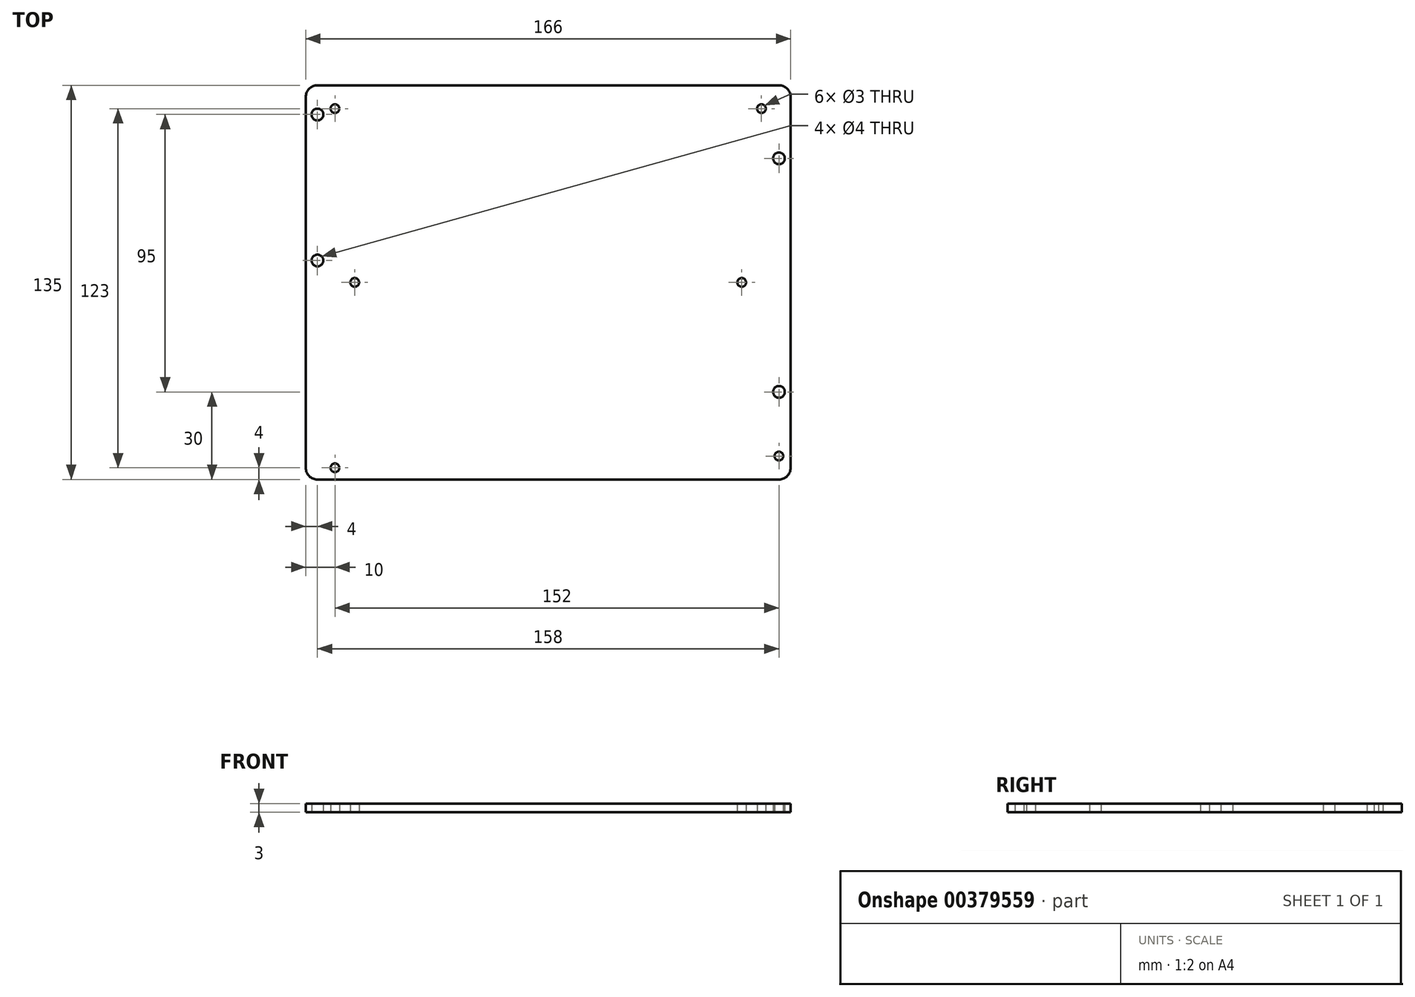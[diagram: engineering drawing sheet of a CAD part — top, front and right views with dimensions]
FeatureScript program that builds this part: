
annotation { "Feature Type Name" : "Feature", "Feature Type Description" : "" }
export const myFeature = defineFeature(function(context is Context, id is Id, definition is map)
    precondition{}
    {
        {
            var Q0;
            Q0=qCreatedBy(makeId("Top.planeOp"),FACE);
            var sketch = newSketch(context, id + "F0", { "sketchPlane" : qUnion([Q0])});
            skLineSegment(sketch, "E0.bottom", {"start": v(79, 67.5) * mm, "end": v(-79, 67.5) * mm});
            skLineSegment(sketch, "E0.top", {"start": v(79, -67.5) * mm, "end": v(-79, -67.5) * mm});
            skLineSegment(sketch, "E0.left", {"start": v(83, 63.5) * mm, "end": v(83, -63.5) * mm});
            skLineSegment(sketch, "E0.right", {"start": v(-83, 63.5) * mm, "end": v(-83, -63.5) * mm});
            skPoint(sketch, "E0.middle", {"position": v(0, 0) * mm});
            skLineSegment(sketch, "E1", {"start": v(0, 86.64) * mm, "end": v(0, -82.26) * mm, "construction": true});
            skLineSegment(sketch, "E2", {"start": v(-88.3, 0) * mm, "end": v(88.19, 0) * mm, "construction": true});
            skPoint(sketch, "E2.endSnap0", {"position": v(-83, 0) * mm});
            skLineSegment(sketch, "E3", {"start": v(-79, 72) * mm, "end": v(-79, -72.22) * mm, "construction": true});
            skLineSegment(sketch, "E4.MirrorCS", {"start": v(79, 72) * mm, "end": v(79, -72.22) * mm, "construction": true});
            skCircle(sketch, "E5", {"center": v(-79, 57.5) * mm, "radius": 2 * mm});
            skCircle(sketch, "E6", {"center": v(-79, 7.5) * mm, "radius": 2 * mm});
            skCircle(sketch, "E7", {"center": v(79, 42.5) * mm, "radius": 2 * mm});
            skCircle(sketch, "E8", {"center": v(79, -37.5) * mm, "radius": 2 * mm});
            skPoint(sketch, "E9.visualSharp", {"position": v(-83, 67.5) * mm});
            skArc(sketch, "E9.filletArc", {"start": v(-79, 67.5) * mm, "mid": v(-81.83, 66.33) * mm, "end": v(-83, 63.5) * mm});
            skPoint(sketch, "E10.visualSharp", {"position": v(83, 67.5) * mm});
            skArc(sketch, "E10.filletArc", {"start": v(83, 63.5) * mm, "mid": v(81.83, 66.33) * mm, "end": v(79, 67.5) * mm});
            skPoint(sketch, "E11.visualSharp", {"position": v(83, -67.5) * mm});
            skArc(sketch, "E11.filletArc", {"start": v(79, -67.5) * mm, "mid": v(81.83, -66.33) * mm, "end": v(83, -63.5) * mm});
            skPoint(sketch, "E12.visualSharp", {"position": v(-83, -67.5) * mm});
            skArc(sketch, "E12.filletArc", {"start": v(-83, -63.5) * mm, "mid": v(-81.83, -66.33) * mm, "end": v(-79, -67.5) * mm});
            skLineSegment(sketch, "E13", {"start": v(-66.25, 72.05) * mm, "end": v(-66.25, -71.65) * mm, "construction": true});
            skLineSegment(sketch, "E14.MirrorCS", {"start": v(66.25, 72.05) * mm, "end": v(66.25, -71.65) * mm, "construction": true});
            skCircle(sketch, "E15", {"center": v(-66.25, 0) * mm, "radius": 1.5 * mm});
            skCircle(sketch, "E16", {"center": v(66.25, 0) * mm, "radius": 1.5 * mm});
            skLineSegment(sketch, "E17", {"start": v(-102.58, 59.5) * mm, "end": v(96.74, 59.5) * mm, "construction": true});
            skLineSegment(sketch, "E18", {"start": v(-73, 75.7) * mm, "end": v(-73, -81.88) * mm, "construction": true});
            skLineSegment(sketch, "E19.MirrorCS", {"start": v(73, 75.7) * mm, "end": v(73, -81.88) * mm, "construction": true});
            skLineSegment(sketch, "E20.MirrorCS", {"start": v(-102.58, -59.5) * mm, "end": v(96.74, -59.5) * mm, "construction": true});
            skCircle(sketch, "E21", {"center": v(-73, 59.5) * mm, "radius": 1.5 * mm});
            skCircle(sketch, "E22.MirrorC", {"center": v(73, 59.5) * mm, "radius": 1.5 * mm});
            skCircle(sketch, "E23.MirrorC", {"center": v(-73, -63.5) * mm, "radius": 1.5 * mm});
            skCircle(sketch, "E24.MirrorC", {"center": v(79, -59.5) * mm, "radius": 1.5 * mm});
            skSolve(sketch);
        }
        {
            var Q0;
            Q0 = qSketchRegion(id + "F0", true);
            extrude(context, id + "F1", {"entities" : qUnion([Q0]), "depth" : 3 * mm});
        }
    });
